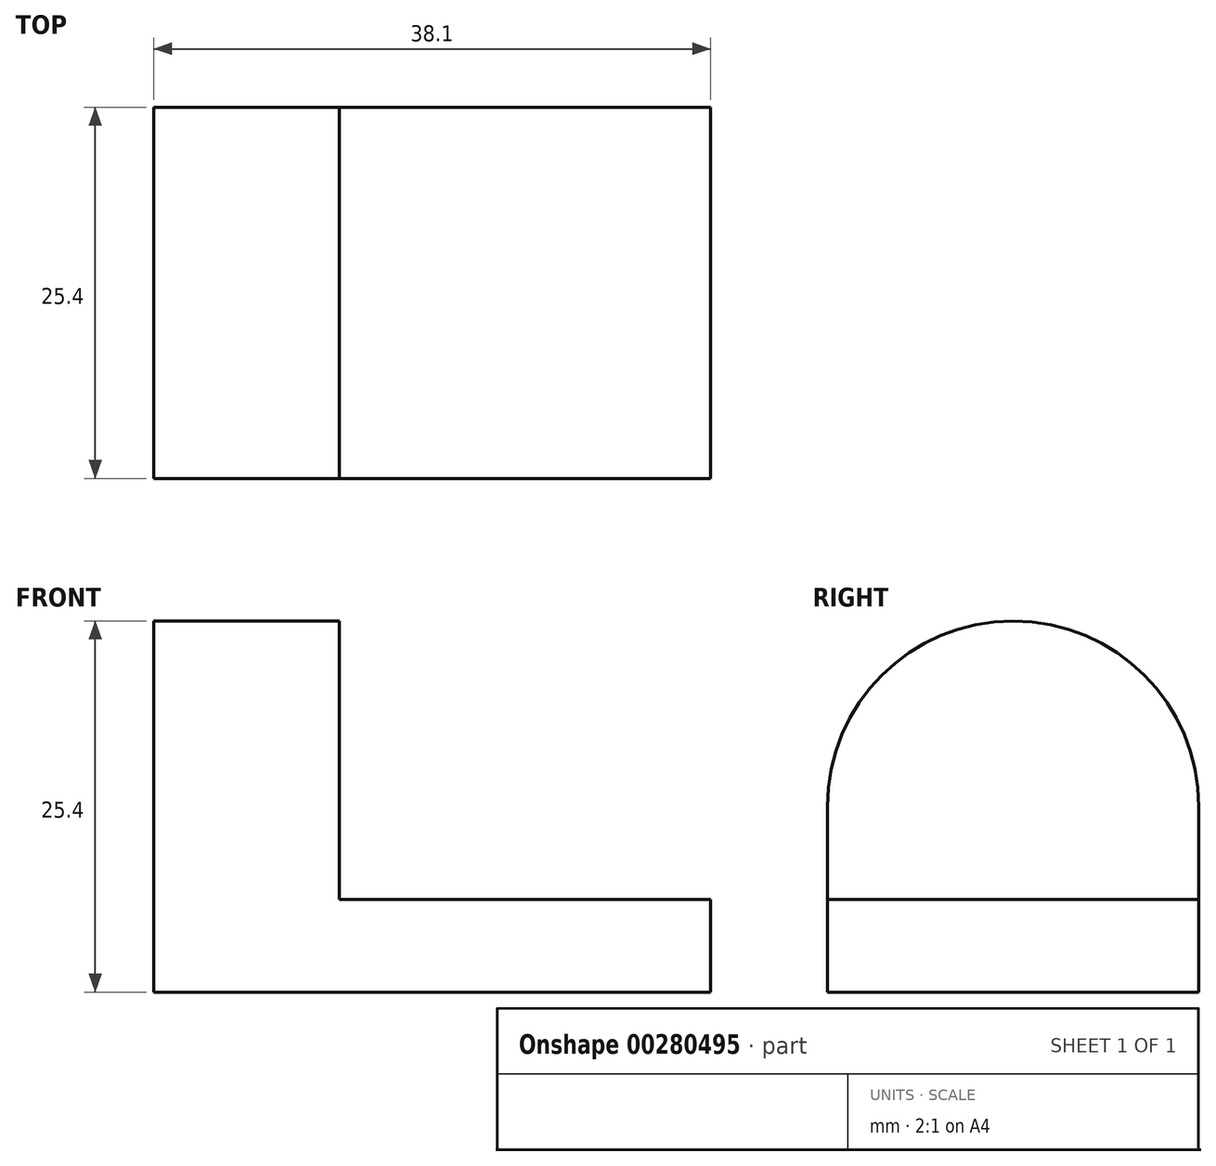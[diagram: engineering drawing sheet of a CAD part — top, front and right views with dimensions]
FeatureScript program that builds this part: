
annotation { "Feature Type Name" : "Feature", "Feature Type Description" : "" }
export const myFeature = defineFeature(function(context is Context, id is Id, definition is map)
    precondition{}
    {
        {
            var Q0;
            Q0=qCreatedBy(makeId("Right.planeOp"),FACE);
            var sketch = newSketch(context, id + "F0", { "sketchPlane" : qUnion([Q0])});
            skLineSegment(sketch, "E0", {"start": v(-12.7, 0) * mm, "end": v(12.7, 0) * mm});
            skLineSegment(sketch, "E1", {"start": v(12.7, 0) * mm, "end": v(12.7, 6.35) * mm});
            skLineSegment(sketch, "E2", {"start": v(12.7, 6.35) * mm, "end": v(-12.7, 6.35) * mm});
            skLineSegment(sketch, "E3", {"start": v(-12.7, 6.35) * mm, "end": v(-12.7, 0) * mm});
            skLineSegment(sketch, "E4", {"start": v(-12.7, 6.35) * mm, "end": v(-12.7, 12.7) * mm});
            skLineSegment(sketch, "E5", {"start": v(12.7, 6.35) * mm, "end": v(12.7, 12.7) * mm});
            skArc(sketch, "E6", {"start": v(-12.7, 12.7) * mm, "mid": v(0, 25.4) * mm, "end": v(12.7, 12.7) * mm});
            skSolve(sketch);
        }
        {
            var Q0;
            Q0=makeQuery(id+"F0.imprint","IMPRINT",FACE,{"disambiguationData":[TD([[makeQuery(id+"F0.imprint","IMPRINT",EDGE,{"derivedFrom":sQuery(id+"F0.wireOp",EDGE,"E0")}),1.0]])]});
            extrude(context, id + "F1", {"entities" : qUnion([Q0]), "endBound" : BoundingType.SYMMETRIC, "depth" : 38.1 * mm});
        }
        {
            var Q0;
            Q0=makeQuery(id+"F0.imprint","IMPRINT",FACE,{"disambiguationData":[TD([[makeQuery(id+"F0.imprint","IMPRINT",EDGE,{"derivedFrom":sQuery(id+"F0.wireOp",EDGE,"E2")}),-1.0]])]});
            extrude(context, id + "F2", {"entities" : qUnion([Q0]), "operationType" : NewBodyOperationType.ADD, "oppositeDirection" : true, "depth" : 19.05 * mm, "hasSecondDirection" : true, "secondDirectionOppositeDirection" : true, "secondDirectionDepth" : 6.35 * mm});
        }
    });
